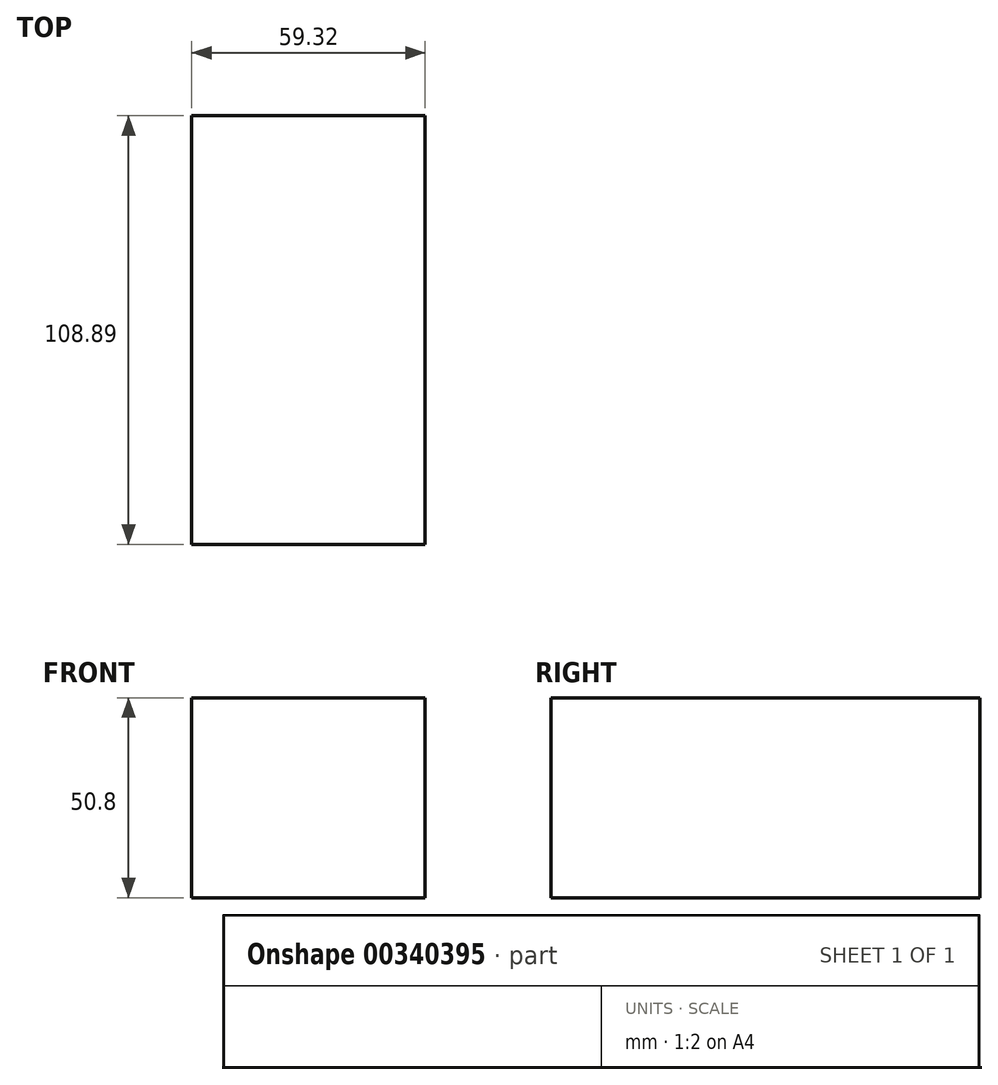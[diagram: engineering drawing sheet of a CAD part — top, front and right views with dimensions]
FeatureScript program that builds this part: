
annotation { "Feature Type Name" : "Feature", "Feature Type Description" : "" }
export const myFeature = defineFeature(function(context is Context, id is Id, definition is map)
    precondition{}
    {
        {
            var Q0;
            Q0=qCreatedBy(makeId("Top.planeOp"),FACE);
            var sketch = newSketch(context, id + "F0", { "sketchPlane" : qUnion([Q0])});
            skLineSegment(sketch, "E0.bottom", {"start": v(0, 108.9) * mm, "end": v(59.32, 108.9) * mm});
            skLineSegment(sketch, "E0.top", {"start": v(0, 0) * mm, "end": v(59.32, 0) * mm});
            skLineSegment(sketch, "E0.left", {"start": v(0, 108.9) * mm, "end": v(0, 0) * mm});
            skLineSegment(sketch, "E0.right", {"start": v(59.32, 108.9) * mm, "end": v(59.32, 0) * mm});
            skSolve(sketch);
        }
        {
            var Q0;
            Q0 = qSketchRegion(id + "F0", true);
            extrude(context, id + "F1", {"entities" : qUnion([Q0]), "depth" : 50.8 * mm});
        }
    });
